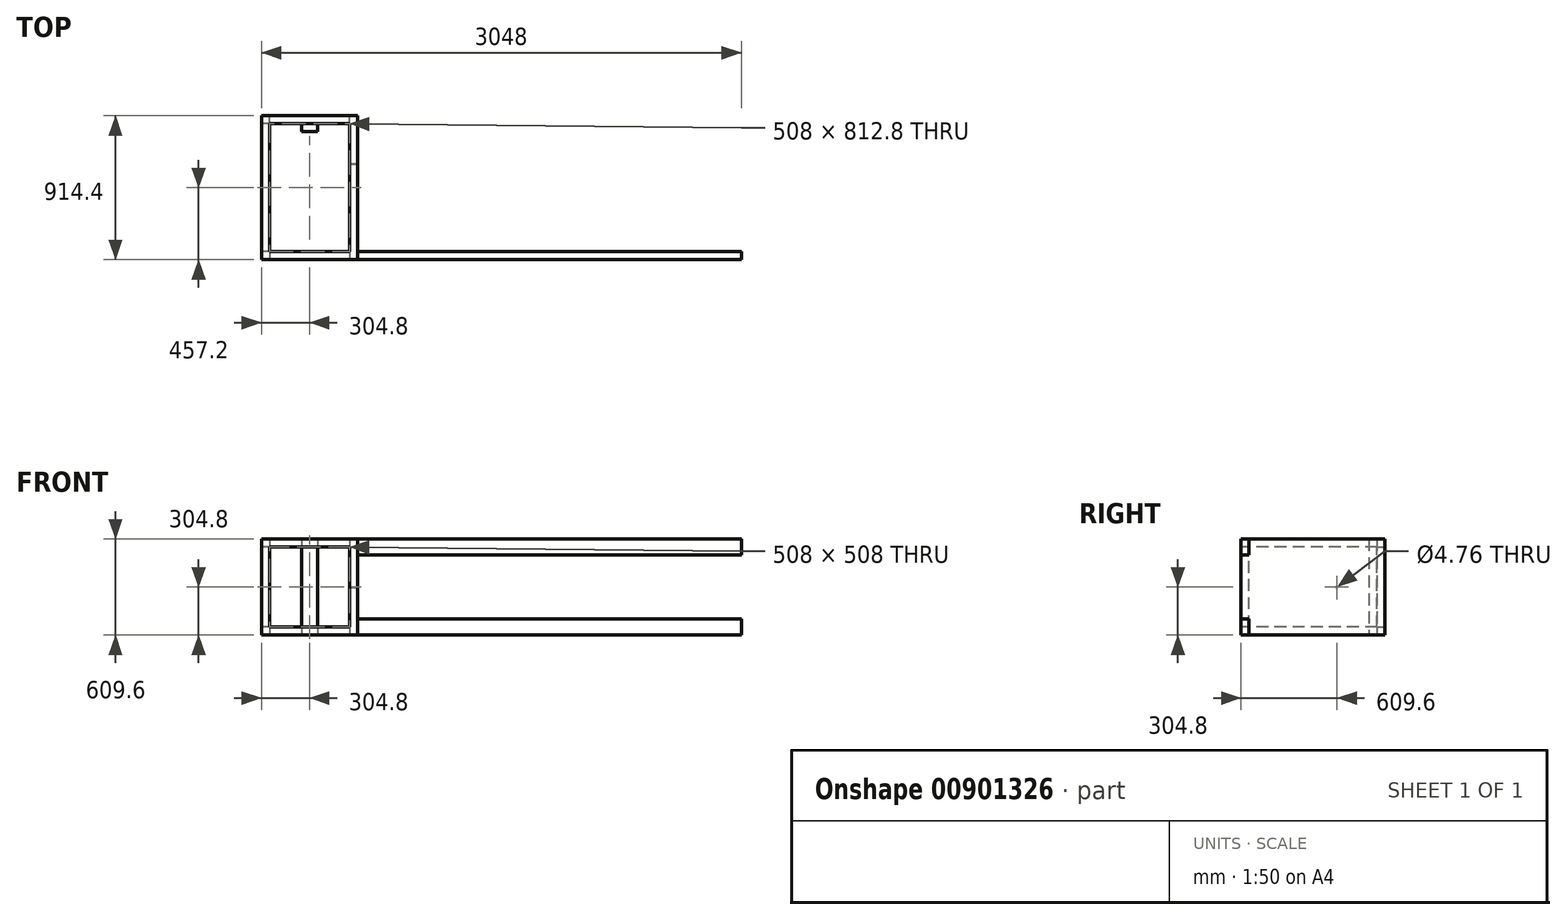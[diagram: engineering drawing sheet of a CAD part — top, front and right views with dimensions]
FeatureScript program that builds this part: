
annotation { "Feature Type Name" : "Feature", "Feature Type Description" : "" }
export const myFeature = defineFeature(function(context is Context, id is Id, definition is map)
    precondition{}
    {
        {
            var Q0;
            Q0=qCreatedBy(makeId("Top.planeOp"),FACE);
            var sketch = newSketch(context, id + "F0", { "sketchPlane" : qUnion([Q0])});
            skLineSegment(sketch, "E0.bottom", {"start": v(304.8, -457.2) * mm, "end": v(-304.8, -457.2) * mm});
            skLineSegment(sketch, "E0.top", {"start": v(304.8, 457.2) * mm, "end": v(-304.8, 457.2) * mm});
            skLineSegment(sketch, "E0.left", {"start": v(304.8, -457.2) * mm, "end": v(304.8, 457.2) * mm});
            skLineSegment(sketch, "E0.right", {"start": v(-304.8, -457.2) * mm, "end": v(-304.8, 457.2) * mm});
            skPoint(sketch, "E0.middle", {"position": v(0, 0) * mm});
            skLineSegment(sketch, "E1.bottom", {"start": v(254, -406.4) * mm, "end": v(-254, -406.4) * mm});
            skLineSegment(sketch, "E1.top", {"start": v(254, 406.4) * mm, "end": v(-254, 406.4) * mm});
            skLineSegment(sketch, "E1.left", {"start": v(254, -406.4) * mm, "end": v(254, 406.4) * mm});
            skLineSegment(sketch, "E1.right", {"start": v(-254, -406.4) * mm, "end": v(-254, 406.4) * mm});
            skSolve(sketch);
        }
        {
            var Q0;
            Q0=makeQuery(id+"F0.imprint","IMPRINT",FACE,{"disambiguationData":[TD([[makeQuery(id+"F0.imprint","IMPRINT",EDGE,{"derivedFrom":sQuery(id+"F0.wireOp",EDGE,"E0.bottom")}),-1.0]])]});
            extrude(context, id + "F1", {"entities" : qUnion([Q0]), "depth" : 609.6 * mm, "offsetDistance" : 25.4 * mm});
        }
        {
            var Q0;
            Q0=makeQuery(id+"F1.opExtrude","SWEPT_FACE",FACE,{"disambiguationData":[OSD([sQuery(id+"F0.wireOp",EDGE,"E0.top")])]});
            var sketch = newSketch(context, id + "F2", { "sketchPlane" : qUnion([Q0])});
            skLineSegment(sketch, "E2", {"start": v(0, 609.6) * mm, "end": v(0, 0) * mm, "construction": true});
            skLineSegment(sketch, "E3", {"start": v(304.8, 304.8) * mm, "end": v(-304.8, 304.8) * mm, "construction": true});
            skLineSegment(sketch, "E4.bottom", {"start": v(-254, 50.8) * mm, "end": v(254, 50.8) * mm});
            skLineSegment(sketch, "E4.top", {"start": v(-254, 558.8) * mm, "end": v(254, 558.8) * mm});
            skLineSegment(sketch, "E4.left", {"start": v(-254, 50.8) * mm, "end": v(-254, 558.8) * mm});
            skLineSegment(sketch, "E4.right", {"start": v(254, 50.8) * mm, "end": v(254, 558.8) * mm});
            skPoint(sketch, "E4.middle", {"position": v(0, 304.8) * mm});
            skSolve(sketch);
        }
        {
            var Q0;
            Q0=makeQuery(id+"F2.imprint","IMPRINT",FACE,{"disambiguationData":[TD([[makeQuery(id+"F2.imprint","IMPRINT",EDGE,{"derivedFrom":sQuery(id+"F2.wireOp",EDGE,"E4.bottom")}),1.0]])]});
            extrude(context, id + "F3", {"entities" : qUnion([Q0]), "operationType" : NewBodyOperationType.REMOVE, "oppositeDirection" : true, "depth" : 50.8 * mm, "offsetDistance" : 25.4 * mm});
        }
        {
            var Q0;
            Q0=makeQuery(id+"F1.opExtrude","SWEPT_FACE",FACE,{"disambiguationData":[OSD([sQuery(id+"F0.wireOp",EDGE,"E0.bottom")])]});
            var sketch = newSketch(context, id + "F4", { "sketchPlane" : qUnion([Q0])});
            skLineSegment(sketch, "E5", {"start": v(-304.8, 304.8) * mm, "end": v(304.8, 304.8) * mm, "construction": true});
            skLineSegment(sketch, "E6", {"start": v(0, 0) * mm, "end": v(0, 609.6) * mm, "construction": true});
            skLineSegment(sketch, "E7.bottom", {"start": v(254, 558.8) * mm, "end": v(-254, 558.8) * mm});
            skLineSegment(sketch, "E7.top", {"start": v(254, 50.8) * mm, "end": v(-254, 50.8) * mm});
            skLineSegment(sketch, "E7.left", {"start": v(254, 558.8) * mm, "end": v(254, 50.8) * mm});
            skLineSegment(sketch, "E7.right", {"start": v(-254, 558.8) * mm, "end": v(-254, 50.8) * mm});
            skPoint(sketch, "E7.middle", {"position": v(0, 304.8) * mm});
            skSolve(sketch);
        }
        {
            var Q0;
            Q0=makeQuery(id+"F4.imprint","IMPRINT",FACE,{"disambiguationData":[TD([[makeQuery(id+"F4.imprint","IMPRINT",EDGE,{"derivedFrom":sQuery(id+"F4.wireOp",EDGE,"E7.bottom")}),1.0]])]});
            extrude(context, id + "F5", {"entities" : qUnion([Q0]), "operationType" : NewBodyOperationType.REMOVE, "oppositeDirection" : true, "depth" : 50.8 * mm, "offsetDistance" : 25.4 * mm});
        }
        {
            var Q0;
            Q0=makeQuery(id+"F1.opExtrude","SWEPT_FACE",FACE,{"disambiguationData":[OSD([sQuery(id+"F0.wireOp",EDGE,"E0.right")])]});
            var sketch = newSketch(context, id + "F6", { "sketchPlane" : qUnion([Q0])});
            skLineSegment(sketch, "E8", {"start": v(457.2, 304.8) * mm, "end": v(-457.2, 304.8) * mm, "construction": true});
            skLineSegment(sketch, "E9", {"start": v(0, 609.6) * mm, "end": v(0, 0) * mm, "construction": true});
            skLineSegment(sketch, "E10.bottom", {"start": v(-406.4, 50.8) * mm, "end": v(406.4, 50.8) * mm});
            skLineSegment(sketch, "E10.top", {"start": v(-406.4, 558.8) * mm, "end": v(406.4, 558.8) * mm});
            skLineSegment(sketch, "E10.left", {"start": v(-406.4, 50.8) * mm, "end": v(-406.4, 558.8) * mm});
            skLineSegment(sketch, "E10.right", {"start": v(406.4, 50.8) * mm, "end": v(406.4, 558.8) * mm});
            skPoint(sketch, "E10.middle", {"position": v(0, 304.8) * mm});
            skSolve(sketch);
        }
        {
            var Q0;
            Q0=makeQuery(id+"F6.imprint","IMPRINT",FACE,{"disambiguationData":[TD([[makeQuery(id+"F6.imprint","IMPRINT",EDGE,{"derivedFrom":sQuery(id+"F6.wireOp",EDGE,"E10.bottom")}),1.0]])]});
            extrude(context, id + "F7", {"entities" : qUnion([Q0]), "operationType" : NewBodyOperationType.REMOVE, "oppositeDirection" : true, "depth" : 50.8 * mm, "offsetDistance" : 25.4 * mm});
        }
        {
            var Q0;
            Q0=makeQuery(id+"F1.opExtrude","SWEPT_FACE",FACE,{"disambiguationData":[OSD([sQuery(id+"F0.wireOp",EDGE,"E0.left")])]});
            var sketch = newSketch(context, id + "F8", { "sketchPlane" : qUnion([Q0])});
            skLineSegment(sketch, "E11", {"start": v(-406.4, 609.6) * mm, "end": v(-406.4, 0) * mm});
            skLineSegment(sketch, "E12", {"start": v(-457.2, 508) * mm, "end": v(-406.4, 508) * mm});
            skLineSegment(sketch, "E13", {"start": v(-457.2, 101.6) * mm, "end": v(-406.4, 101.6) * mm});
            skLineSegment(sketch, "E14", {"start": v(457.2, 304.8) * mm, "end": v(-457.2, 304.8) * mm, "construction": true});
            skPoint(sketch, "E15", {"position": v(152.4, 304.8) * mm});
            skSolve(sketch);
        }
        {
            var Q0;
            {var subQ4=sQuery(id+"F8.wireOp",EDGE,"E12");Q0=makeQuery(id+"F8.imprint","IMPRINT",FACE,{"disambiguationData":[TD([[makeQuery(id+"F8.imprint","IMPRINT",EDGE,{"derivedFrom":subQ4}),1.0]])]});}
            var Q1;
            {var subQ4=sQuery(id+"F8.wireOp",EDGE,"E13");Q1=makeQuery(id+"F8.imprint","IMPRINT",FACE,{"disambiguationData":[TD([[makeQuery(id+"F8.imprint","IMPRINT",EDGE,{"derivedFrom":subQ4}),-1.0]])]});}
            extrude(context, id + "F9", {"entities" : qUnion([Q0, Q1]), "depth" : 2438.4 * mm, "offsetDistance" : 25.4 * mm});
        }
        {
            var Q0;
            Q0=sQuery(id+"F8.wireOp",VERTEX,"E15");
            var Q1;
            Q1=makeQuery(id+"F1.opExtrude","SWEPT_BODY",BODY,{"disambiguationData":[OSD([sQuery(id+"F0.wireOp",EDGE,"E0.bottom"),sQuery(id+"F0.wireOp",EDGE,"E0.top"),sQuery(id+"F0.wireOp",EDGE,"E0.left"),sQuery(id+"F0.wireOp",EDGE,"E0.right"),sQuery(id+"F0.wireOp",EDGE,"E1.bottom"),sQuery(id+"F0.wireOp",EDGE,"E1.top"),sQuery(id+"F0.wireOp",EDGE,"E1.left"),sQuery(id+"F0.wireOp",EDGE,"E1.right")])]});
            hole(context, id + "F10", {"style" : HoleStyle.SIMPLE, "endStyle" : HoleEndStyle.THROUGH, "holeDiameter" : 4.76 * mm, "majorDiameter" : 6.35 * mm, "isTappedThrough" : true, "tappedDepth" : 12.7 * mm, "tapClearance" : 3, "locations" : qUnion([Q0]), "scope" : qUnion([Q1])});
        }
        {
            var Q0;
            {var subQ2=sQuery(id+"F0.wireOp",EDGE,"E1.top");Q0=makeQuery(id+"F3.boolean.opBoolean","SPLIT",FACE,{"disambiguationData":[TD([makeQuery(id+"F3.opExtrude","SWEPT_FACE",FACE,{"disambiguationData":[OSD([sQuery(id+"F2.wireOp",EDGE,"E4.bottom")])]})])],"derivedFrom":makeQuery(id+"F1.opExtrude","SWEPT_FACE",FACE,{"disambiguationData":[OSD([subQ2])]})});}
            var sketch = newSketch(context, id + "F11", { "sketchPlane" : qUnion([Q0])});
            skLineSegment(sketch, "E16", {"start": v(0, 0) * mm, "end": v(0, 609.6) * mm, "construction": true});
            skLineSegment(sketch, "E17.bottom", {"start": v(-50.8, 609.6) * mm, "end": v(50.8, 609.6) * mm});
            skLineSegment(sketch, "E17.top", {"start": v(-50.8, 0) * mm, "end": v(50.8, 0) * mm});
            skLineSegment(sketch, "E17.left", {"start": v(-50.8, 609.6) * mm, "end": v(-50.8, 0) * mm});
            skLineSegment(sketch, "E17.right", {"start": v(50.8, 609.6) * mm, "end": v(50.8, 0) * mm});
            skPoint(sketch, "E17.middle", {"position": v(0, 304.8) * mm});
            skSolve(sketch);
        }
        {
            var Q0;
            {var subQ0=sQuery(id+"F11.wireOp",EDGE,"E17.bottom");Q0=makeQuery(id+"F11.imprint","IMPRINT",FACE,{"disambiguationData":[TD([[makeQuery(id+"F11.imprint","IMPRINT",EDGE,{"derivedFrom":subQ0}),-1.0]])]});}
            var Q1;
            {var subQ0=sQuery(id+"F11.wireOp",EDGE,"E17.top");Q1=makeQuery(id+"F11.imprint","IMPRINT",FACE,{"disambiguationData":[TD([[makeQuery(id+"F11.imprint","IMPRINT",EDGE,{"derivedFrom":subQ0}),-1.0]])]});}
            extrude(context, id + "F12", {"entities" : qUnion([Q0, Q1]), "depth" : 50.8 * mm, "offsetDistance" : 25.4 * mm});
        }
    });
